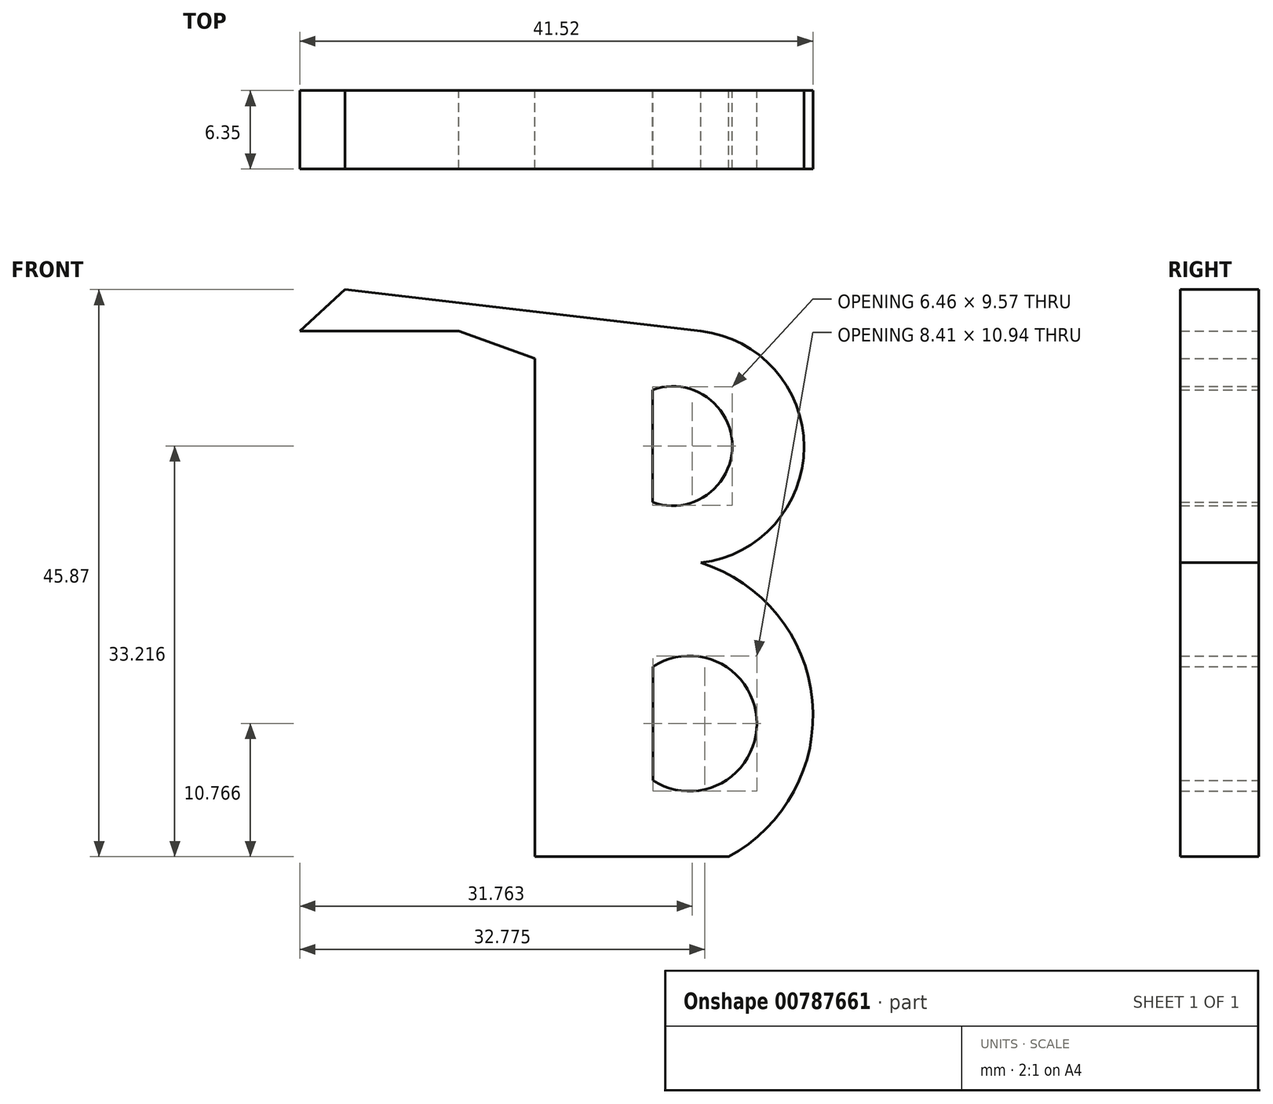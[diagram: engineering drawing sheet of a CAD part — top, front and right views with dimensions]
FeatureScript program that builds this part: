
annotation { "Feature Type Name" : "Feature", "Feature Type Description" : "" }
export const myFeature = defineFeature(function(context is Context, id is Id, definition is map)
    precondition{}
    {
        {
            var Q0;
            Q0=qCreatedBy(makeId("Front.planeOp"),FACE);
            var sketch = newSketch(context, id + "F0", { "sketchPlane" : qUnion([Q0])});
            skLineSegment(sketch, "E0", {"start": v(-24.76, 11.6) * mm, "end": v(-24.76, -28.67) * mm});
            skLineSegment(sketch, "E1", {"start": v(-24.76, 11.6) * mm, "end": v(-30.91, 13.85) * mm});
            skLineSegment(sketch, "E2", {"start": v(-30.91, 13.85) * mm, "end": v(-43.78, 13.85) * mm});
            skLineSegment(sketch, "E3", {"start": v(-43.78, 13.85) * mm, "end": v(-40.14, 17.2) * mm});
            skLineSegment(sketch, "E4", {"start": v(-40.14, 17.2) * mm, "end": v(-11.33, 13.85) * mm});
            skPoint(sketch, "E4.endSnap0", {"position": v(-37.35, 13.85) * mm});
            skArc(sketch, "E5", {"start": v(-11.33, -4.9) * mm, "mid": v(-2.99, 4.48) * mm, "end": v(-11.33, 13.85) * mm});
            skLineSegment(sketch, "E6", {"start": v(-15.25, 9.1) * mm, "end": v(-15.25, 0) * mm});
            skArc(sketch, "E7", {"start": v(-15.25, 0) * mm, "mid": v(-8.79, 4.55) * mm, "end": v(-15.25, 9.1) * mm});
            skArc(sketch, "E8", {"start": v(-9.1, -28.67) * mm, "mid": v(-2.31, -16.04) * mm, "end": v(-11.33, -4.9) * mm});
            skLineSegment(sketch, "E9", {"start": v(-24.76, -28.67) * mm, "end": v(-9.1, -28.67) * mm});
            skLineSegment(sketch, "E10", {"start": v(-15.21, -13.29) * mm, "end": v(-15.21, -22.52) * mm});
            skArc(sketch, "E11", {"start": v(-15.21, -22.52) * mm, "mid": v(-6.8, -17.9) * mm, "end": v(-15.21, -13.29) * mm});
            skSolve(sketch);
        }
        {
            var Q0;
            Q0=makeQuery(id+"F0.imprint","IMPRINT",FACE,{"disambiguationData":[TD([[makeQuery(id+"F0.imprint","IMPRINT",EDGE,{"derivedFrom":sQuery(id+"F0.wireOp",EDGE,"E0")}),1.0]])]});
            extrude(context, id + "F1", {"entities" : qUnion([Q0]), "depth" : 6.35 * mm, "offsetDistance" : 25.4 * mm});
        }
    });
